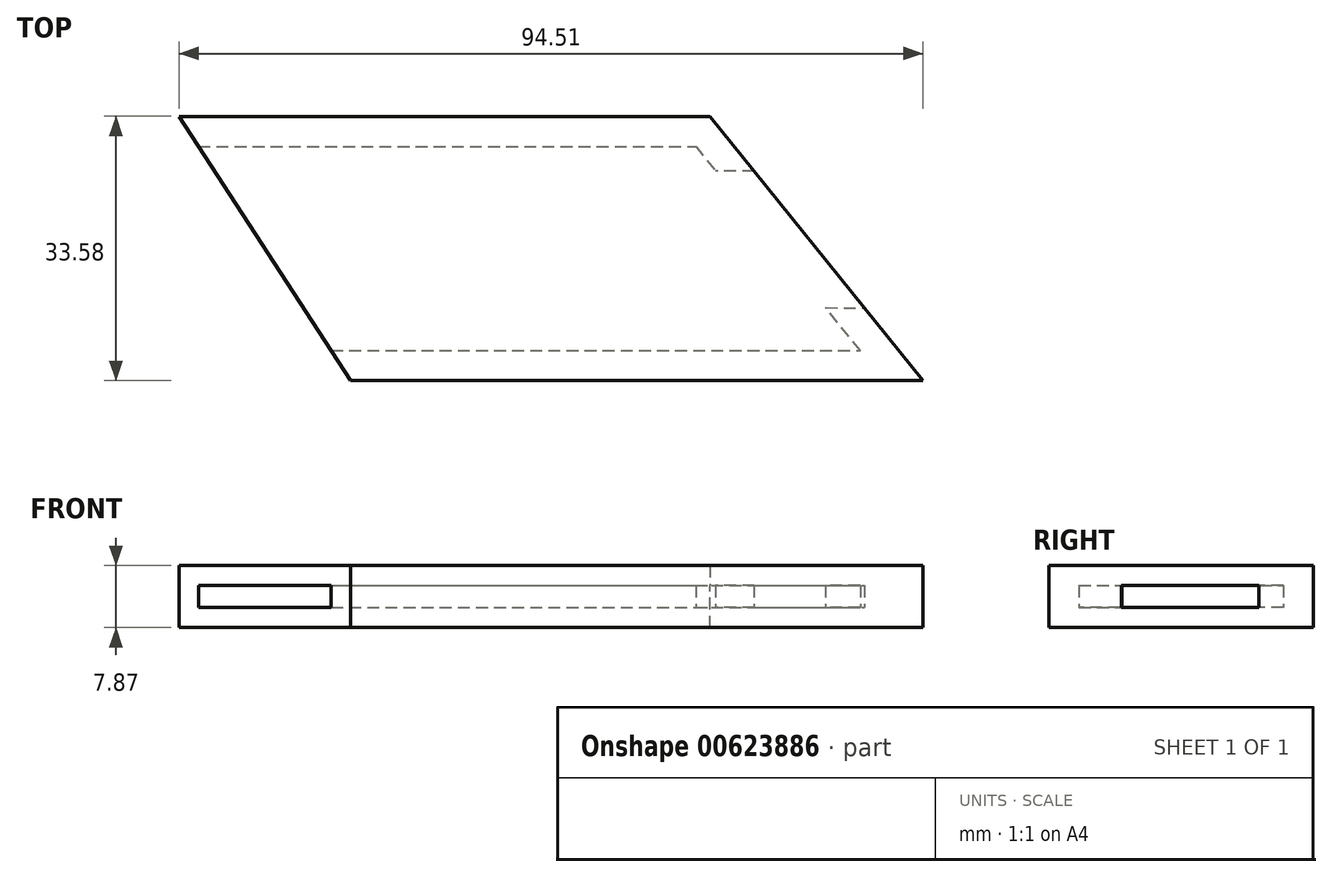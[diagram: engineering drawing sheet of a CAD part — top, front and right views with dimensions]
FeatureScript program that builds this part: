
annotation { "Feature Type Name" : "Feature", "Feature Type Description" : "" }
export const myFeature = defineFeature(function(context is Context, id is Id, definition is map)
    precondition{}
    {
        {
            var Q0;
            Q0=qCreatedBy(makeId("Top.planeOp"),FACE);
            var sketch = newSketch(context, id + "F0", { "sketchPlane" : qUnion([Q0])});
            skLineSegment(sketch, "E0.0", {"start": v(49.03, -18.3) * mm, "end": v(53.06, -23.32) * mm});
            skLineSegment(sketch, "E0.1", {"start": v(-19.64, -23.32) * mm, "end": v(53.06, -23.32) * mm});
            skLineSegment(sketch, "E1.0", {"start": v(24.2, 6.45) * mm, "end": v(26.72, 3.33) * mm});
            skLineSegment(sketch, "E2.0", {"start": v(-22.11, -19.5) * mm, "end": v(45.1, -19.5) * mm});
            skLineSegment(sketch, "E3", {"start": v(49.03, -18.3) * mm, "end": v(45.65, -14.11) * mm});
            skLineSegment(sketch, "E4.0", {"start": v(45.1, -19.5) * mm, "end": v(43.16, -17.1) * mm});
            skLineSegment(sketch, "E5", {"start": v(45.1, -19.5) * mm, "end": v(40.7, -14.04) * mm});
            skLineSegment(sketch, "E6", {"start": v(40.7, -14.04) * mm, "end": v(45.65, -14.11) * mm});
            skLineSegment(sketch, "E7", {"start": v(31.61, 3.33) * mm, "end": v(26.72, 3.33) * mm});
            skLineSegment(sketch, "E8", {"start": v(-41.45, 10.26) * mm, "end": v(-19.64, -23.32) * mm});
            skLineSegment(sketch, "E9", {"start": v(31.61, 3.33) * mm, "end": v(53.06, -23.32) * mm});
            skLineSegment(sketch, "E10", {"start": v(-41.45, 10.26) * mm, "end": v(26.03, 10.26) * mm});
            skLineSegment(sketch, "E11", {"start": v(-38.98, 6.45) * mm, "end": v(24.2, 6.45) * mm});
            skLineSegment(sketch, "E12", {"start": v(26.03, 10.26) * mm, "end": v(31.61, 3.33) * mm});
            skSolve(sketch);
        }
        {
            var Q0;
            Q0=makeQuery(id+"F0.imprint","IMPRINT",FACE,{"disambiguationData":[TD([[makeQuery(id+"F0.imprint","IMPRINT",EDGE,{"derivedFrom":sQuery(id+"F0.wireOp",EDGE,"E1.0")}),-1.0]])]});
            var Q1;
            Q1=makeQuery(id+"F0.imprint","IMPRINT",FACE,{"disambiguationData":[TD([[makeQuery(id+"F0.imprint","IMPRINT",EDGE,{"derivedFrom":sQuery(id+"F0.wireOp",EDGE,"E1.0")}),1.0]])]});
            var Q2;
            {var subQ4=sQuery(id+"F0.wireOp",EDGE,"E0.1");Q2=makeQuery(id+"F0.imprint","IMPRINT",FACE,{"disambiguationData":[TD([[makeQuery(id+"F0.imprint","IMPRINT",EDGE,{"derivedFrom":subQ4}),1.0]])]});}
            extrude(context, id + "F1", {"entities" : qUnion([Q0, Q1, Q2]), "oppositeDirection" : true, "depth" : 2.54 * mm, "offsetDistance" : 25.4 * mm});
        }
        {
            var Q0;
            Q0=makeQuery(id+"F0.imprint","IMPRINT",FACE,{"disambiguationData":[TD([[makeQuery(id+"F0.imprint","IMPRINT",EDGE,{"derivedFrom":sQuery(id+"F0.wireOp",EDGE,"E1.0")}),1.0]])]});
            var Q1;
            {var subQ4=sQuery(id+"F0.wireOp",EDGE,"E0.1");Q1=makeQuery(id+"F0.imprint","IMPRINT",FACE,{"disambiguationData":[TD([[makeQuery(id+"F0.imprint","IMPRINT",EDGE,{"derivedFrom":subQ4}),1.0]])]});}
            extrude(context, id + "F2", {"entities" : qUnion([Q0, Q1]), "operationType" : NewBodyOperationType.ADD, "depth" : 2.8 * mm, "offsetDistance" : 25.4 * mm});
        }
        {
            var Q0;
            Q0=makeQuery(id+"F2.opExtrude","CAP_FACE",FACE,{"disambiguationData":[OSD([sQuery(id+"F0.wireOp",EDGE,"E1.0"),sQuery(id+"F0.wireOp",EDGE,"E7"),sQuery(id+"F0.wireOp",EDGE,"E8"),sQuery(id+"F0.wireOp",EDGE,"E10"),sQuery(id+"F0.wireOp",EDGE,"E11"),sQuery(id+"F0.wireOp",EDGE,"E12")])],"isStart":false});
            cPlane(context, id + "F3", {"entities" : qUnion([Q0]), "cplaneType" : CPlaneType.OFFSET, "offset" : 0 * mm, "width" : 152.4 * mm, "height" : 152.4 * mm});
        }
        {
            var Q0;
            Q0=qCreatedBy(id+"F3.planeOp",FACE);
            var sketch = newSketch(context, id + "F4", { "sketchPlane" : qUnion([Q0])});
            skLineSegment(sketch, "E13.0", {"start": v(49.03, -18.3) * mm, "end": v(53.06, -23.32) * mm});
            skLineSegment(sketch, "E13.1", {"start": v(-19.64, -23.32) * mm, "end": v(53.06, -23.32) * mm});
            skLineSegment(sketch, "E14.0", {"start": v(24.2, 6.45) * mm, "end": v(26.72, 3.33) * mm});
            skLineSegment(sketch, "E15.0", {"start": v(-22.11, -19.5) * mm, "end": v(45.1, -19.5) * mm});
            skLineSegment(sketch, "E16", {"start": v(49.03, -18.3) * mm, "end": v(45.65, -14.12) * mm});
            skLineSegment(sketch, "E17.0", {"start": v(45.1, -19.5) * mm, "end": v(43.16, -17.1) * mm});
            skLineSegment(sketch, "E18", {"start": v(45.1, -19.5) * mm, "end": v(40.7, -14.05) * mm});
            skLineSegment(sketch, "E19", {"start": v(40.7, -14.05) * mm, "end": v(45.65, -14.12) * mm});
            skLineSegment(sketch, "E20", {"start": v(31.61, 3.33) * mm, "end": v(26.72, 3.33) * mm});
            skLineSegment(sketch, "E21", {"start": v(-41.45, 10.26) * mm, "end": v(-19.64, -23.32) * mm});
            skLineSegment(sketch, "E22", {"start": v(31.61, 3.33) * mm, "end": v(53.06, -23.32) * mm});
            skLineSegment(sketch, "E23", {"start": v(-41.45, 10.26) * mm, "end": v(26.03, 10.26) * mm});
            skLineSegment(sketch, "E24", {"start": v(-38.98, 6.45) * mm, "end": v(24.2, 6.45) * mm});
            skLineSegment(sketch, "E25", {"start": v(26.03, 10.26) * mm, "end": v(31.61, 3.33) * mm});
            skSolve(sketch);
        }
        {
            var Q0;
            Q0 = qSketchRegion(id + "F4", true);
            extrude(context, id + "F5", {"entities" : qUnion([Q0]), "operationType" : NewBodyOperationType.ADD, "depth" : 2.54 * mm, "offsetDistance" : 25.4 * mm});
        }
    });
